# Revit family: IS_iLifeS_T4592_BIM_NL
name_source: partatom
category: Plumbing Fixtures
units: mm (PartAtom-declared; Revit-internal decimal feet)

## family parameters
Always vertical = No
Cut with Voids When Loaded = No
OmniClass Number = 23.45.05.21.11.11
OmniClass Title = Water Operated Water Closets
Part Type = Normal
Room Calculation Point = No
Round Connector Dimension = Use Diameter
Shared = No
Work Plane-Based = No

## types (2) — shared parameters
Accessories = https://www.idealstandard.nl
Afmetingen = 480 x 338 x 353 mm
AfstandsEenheid = Millimeter
AreaUnits = millimetres
AssetType = Fixed
Auteur = Ideal Standard
BIMObjectName = IS_IdealStandard_WC pans_i.lifeS_T4592
BIMobject category = Toilets
BIMobject category code = toilets
BIMobject main category = Sanitary
BIMobject main category code = sanitary
Beschrijvinggarantie = Herstellergarantie
BimObjectNaam = IS_IdealStandard_WC pans_i.lifeS_T4592
Brand = Ideal Standard
Brand url = https://www.idealstandard.nl
Breedte = 353.426368
Category = Sanitary
ConnectionType = Plumbing
CurrencyUnit = €
CurrentRevision = 1
Date of publishing = 27/05/2022
Diepte = 480 mm
DurationUnit = Years
DuurEenheid = Jahre
Edition number = 1
ElementType = Fixed
ExpectedLife = 99
Garantieunits = Jahre
Help = https://www.idealstandard.nl
Hoogte = 337.930778790414
Hulp = https://www.idealstandard.nl
IFC Classification = Sanitary Terminal
IfcExportAs = IfcSanitaryTerminalType
IfcExportType = TOILETPAN
Installatieinstructies = https://www.idealstandard.nl
Installation instructions = https://www.idealstandard.nl
InstallationInstructions = https://www.idealstandard.nl
Lengte = 480 mm
LinearUnits = Millimetres
MaintenanceInformation = https://www.idealstandard.nl
Manufacturer = Ideal Standard
Manufacturer name = Ideal Standard
ManufacturerURL = https://www.idealstandard.nl
Materiaal = Glasiges China
MateriaalWC = Glasiges China
Material = Vitrous China
Material main = Vitrous China
Merk = Ideal Standard
NBS Reference Code = 45-35-70/384
NBS Reference Description = WC pans
Name = WC pans_i.lifeS_T4592_IdealStandard
NettWeight = 21.14
Nettogewicht = 21.14
NominalDepth = 480 mm
NominalHeight = 338 mm
NominalLength = 480 mm
NominalWidth = 353 mm
Normen = WC pans_i.lifeS_T4592_IdealStandard
OmniClass Code = 23-31 19 00
OmniClass Description = Toilets
OppervlakteEenheid = Millimeter
PanMaterial = Glasporzellan
PanMounting = wandhängende WC-Pfanne
PredefinedType = Sanitary
Product Guid = ec06e5b5-8cc0-47f7-a8a4-5a532cfb1517
Product SKU = T4592
Product certification = https://www.idealstandard.nl
Product data url = https://bimobject.com
Product family = I.life S
Product group = Sanitry: WC Pans
Product name = i.life S Wall Hung 48 cm Rim less WC Bowl
Product url = https://www.idealstandard.nl
ProductInformation = https://www.idealstandard.nl
Productinformatie = https://www.idealstandard.nl
QR code = http://bimobject.com
Referentie = i.life S Wall Hung 48 cm Rim less WC Bowl
ReplacementCost = 0
Revisie = 1
Shape = Sculpture
Size = 480 x 338 x 353 mm
Space = Internal
SpareParts = https://www.idealstandard.nl
Technical description = https://www.idealstandard.nl
Telefoonnummer = 077 355 08 08
Typeconnectie = Installation
UNSPSC Code = 301815
URL = https://www.idealstandard.nl
Uniclass 2015 Code = Pr_40_20_93_94
Uniclass 2015 Name = WC pans
Uniclass2015Beschrijving = WC pans
Uniclass2015Code = Pr_40_20_93_94
Uniclass2015Referentie = Pr_40_20_93_94
Uniclass2015Title = WC pans
Uniclass2015Version = v.25
Urlproducent = https://www.idealstandard.nl
ValutaEenheid = Euro
Versie = 1
Version = 1
VolumeUnits = Litres
Volumeunits = Liter
Vorm = geformt
WRASURL = https://www.wrasapprovals.co.uk
WarrantyDescription = manufacturer warranty
WarrantyDurationUnit = years
Wisselstukken = https://www.idealstandard.nl
Youtube clip = https://www.youtube.com
zero-valued in all types: BrutoGewicht, Cost, Vervangingskosten

## per-type parameters (varying)
| type | Afwerking | Artikelnummer | Artikelomschrijving | BarCode | Color | Description | Eigenschappen | Features | Finish | GTIN code | Kleur | MainColor | Model | ModelNumber | ModelReference | PanColor | ToiletPanType | ToiletType |
| T459201 - i.life S Wall Hung 48 cm Rim less WC Bowl - White | Weiß | T459201 | Ideal Standard i.life S, wandhängendes Becken, RimLS+, verdeckte Befestigung, Easyfix+, kompakt 48 cm, im Karton, EU-Palette | 8014140491729 | Weiß | Ideal Standard i.life S, wallhung bowl, RimLS+, hidden fixation, Easyfix+, compact 48 cm, in carton box , EU pallet | Ideal Standard i.life S, wandhängendes Becken, RimLS+, verdeckte Befestigung, Easyfix+, kompakt 48 cm, im Karton, EU-Palette | Ideal Standard i.life S, wallhung bowl, RimLS+, hidden fixation, Easyfix+, compact 48 cm, in carton box , EU pallet | White | https://8014140491729 | Weiß | White | T459201 | T459201 | i.life S Wall Hung 48 cm Rim less WC Bowl | White | Wall Hung WC Pan | Wall Hung WC Pan |
| T4592MA - i.life S Wall Hung, Rim less 48 cm compact WC bowl - Ideal Plus White | Ideales Plus-Weiß | T4592MA | Ideal Standard i.life S, wandhängendes Becken, RimLS+, verdeckte Befestigung, Easyfix+, kompakt 48 cm, weiß Ideal Plus, im Karton, EU-Palette | 8014140491736 | Ideales Plus-Weiß | Ideal Standard i.life S, wallhung bowl, RimLS+, hidden fixation, Easyfix+, compact 48 cm, white Ideal Plus, in carton box , EU pallet | Ideal Standard i.life S, wandhängendes Becken, RimLS+, verdeckte Befestigung, Easyfix+, kompakt 48 cm, weiß Ideal Plus, im Karton, EU-Palette | Ideal Standard i.life S, wallhung bowl, RimLS+, hidden fixation, Easyfix+, compact 48 cm, white Ideal Plus, in carton box , EU pallet | Ideal Plus White | https://8014140491736 | Ideales Plus-Weiß | Ideal Plus White | T4592MA | T4592MA | i.life S Wall Hung, Rim less 48 cm compact WC bowl | Ideal Plus White | Wall Hung Rimless WC Pan | Wall Hung Rimless WC Pan |

## geometry (parser evidence)
native form markers: Sweep x2
no freeform markers — native parametric forms only
